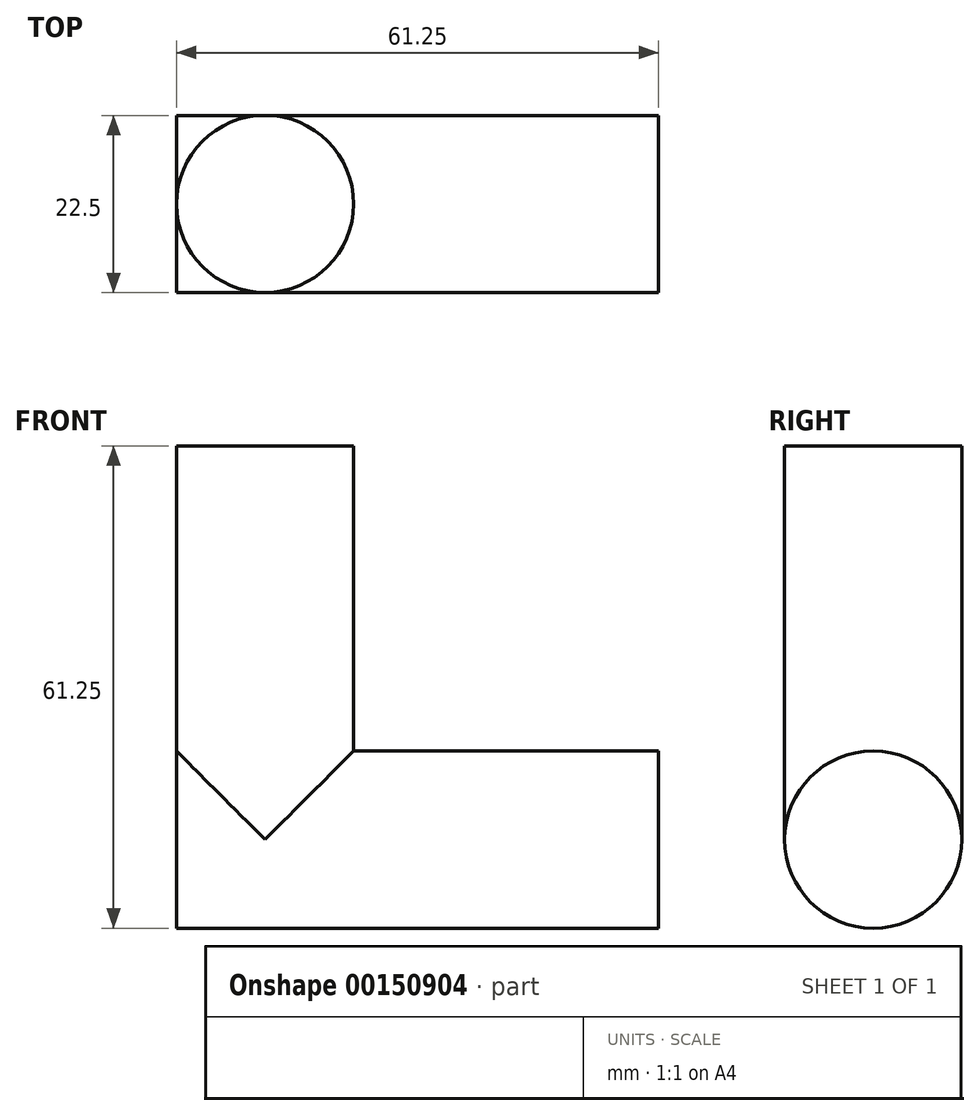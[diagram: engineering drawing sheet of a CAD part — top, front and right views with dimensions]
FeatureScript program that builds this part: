
annotation { "Feature Type Name" : "Feature", "Feature Type Description" : "" }
export const myFeature = defineFeature(function(context is Context, id is Id, definition is map)
    precondition{}
    {
        {
            var Q0;
            Q0=qCreatedBy(makeId("Right.planeOp"),FACE);
            var sketch = newSketch(context, id + "F0", { "sketchPlane" : qUnion([Q0])});
            skCircle(sketch, "E0", {"center": v(0, 0) * mm, "radius": 11.25 * mm});
            skSolve(sketch);
        }
        {
            var Q0;
            Q0=qSketchRegion(id+"F0",true);
            extrude(context, id + "F1", {"entities" : qUnion([Q0]), "depth" : 50 * mm, "hasSecondDirection" : true, "secondDirectionOppositeDirection" : true, "secondDirectionDepth" : 11.25 * mm});
        }
        {
            var Q0;
            Q0=qCreatedBy(makeId("Top.planeOp"),FACE);
            var sketch = newSketch(context, id + "F2", { "sketchPlane" : qUnion([Q0])});
            skCircle(sketch, "E1", {"center": v(0, 0) * mm, "radius": 11.25 * mm});
            skSolve(sketch);
        }
        {
            var Q0;
            Q0=qSketchRegion(id+"F2",true);
            extrude(context, id + "F3", {"entities" : qUnion([Q0]), "operationType" : NewBodyOperationType.ADD, "depth" : 50 * mm});
        }
    });
